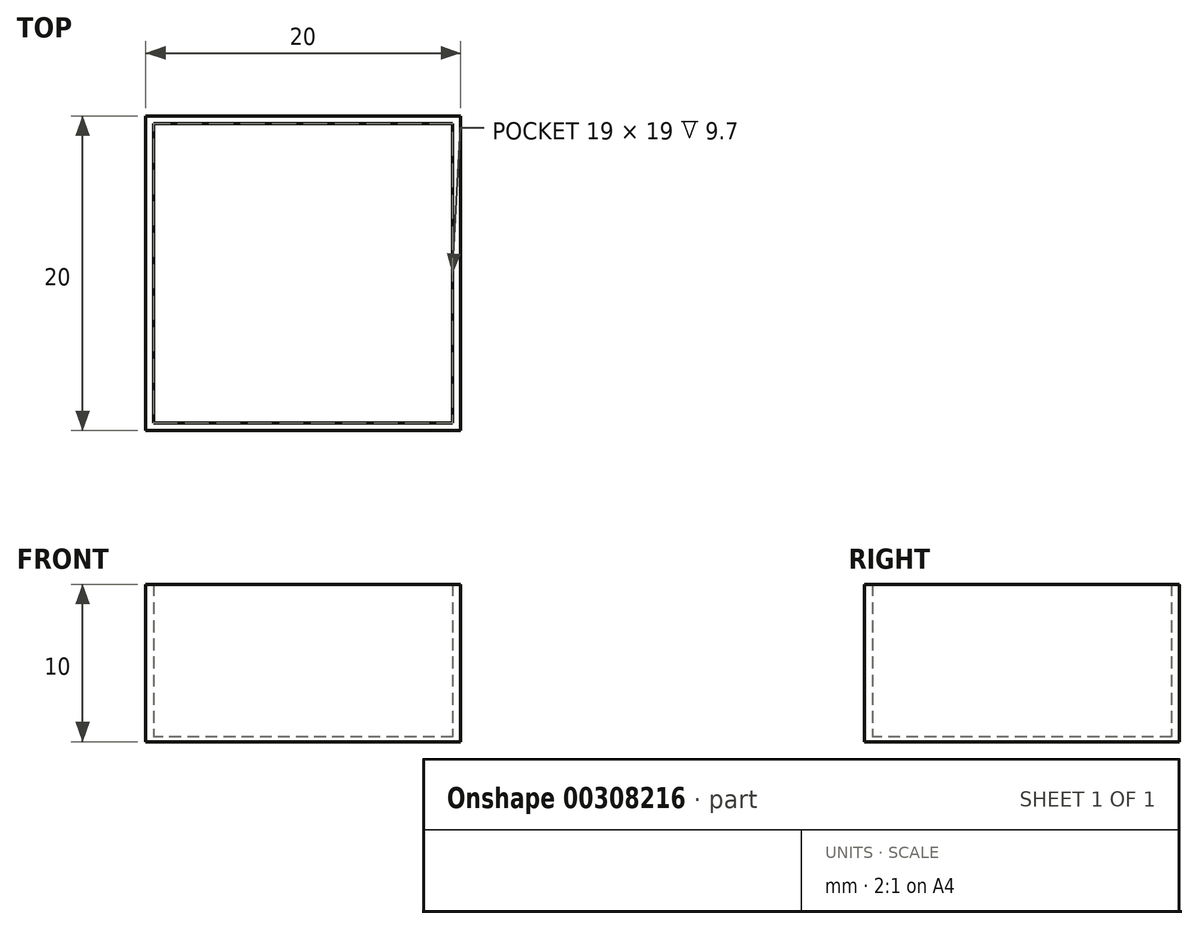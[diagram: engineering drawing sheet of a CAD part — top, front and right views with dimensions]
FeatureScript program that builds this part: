
annotation { "Feature Type Name" : "Feature", "Feature Type Description" : "" }
export const myFeature = defineFeature(function(context is Context, id is Id, definition is map)
    precondition{}
    {
        {
            var Q0;
            Q0=qCreatedBy(makeId("Top.planeOp"),FACE);
            var sketch = newSketch(context, id + "F0", { "sketchPlane" : qUnion([Q0])});
            skLineSegment(sketch, "E0.bottom", {"start": v(10, 10) * mm, "end": v(-10, 10) * mm});
            skLineSegment(sketch, "E0.top", {"start": v(10, -10) * mm, "end": v(-10, -10) * mm});
            skLineSegment(sketch, "E0.left", {"start": v(10, 10) * mm, "end": v(10, -10) * mm});
            skLineSegment(sketch, "E0.right", {"start": v(-10, 10) * mm, "end": v(-10, -10) * mm});
            skPoint(sketch, "E0.middle", {"position": v(0, 0) * mm});
            skLineSegment(sketch, "E1.bottom", {"start": v(9.5, 9.5) * mm, "end": v(-9.5, 9.5) * mm});
            skLineSegment(sketch, "E1.top", {"start": v(9.5, -9.5) * mm, "end": v(-9.5, -9.5) * mm});
            skLineSegment(sketch, "E1.left", {"start": v(9.5, 9.5) * mm, "end": v(9.5, -9.5) * mm});
            skLineSegment(sketch, "E1.right", {"start": v(-9.5, 9.5) * mm, "end": v(-9.5, -9.5) * mm});
            skSolve(sketch);
        }
        {
            var Q0;
            Q0 = qSketchRegion(id + "F0", true);
            extrude(context, id + "F1", {"entities" : qUnion([Q0]), "depth" : 10 * mm, "offsetDistance" : 25 * mm});
        }
        {
            var Q0;
            Q0=makeQuery(id+"F0.imprint","IMPRINT",FACE,{"disambiguationData":[TD([[makeQuery(id+"F0.imprint","IMPRINT",EDGE,{"derivedFrom":sQuery(id+"F0.wireOp",EDGE,"E1.bottom")}),1.0]])]});
            extrude(context, id + "F2", {"entities" : qUnion([Q0]), "operationType" : NewBodyOperationType.ADD, "depth" : .3 * mm, "offsetDistance" : 25 * mm});
        }
    });
